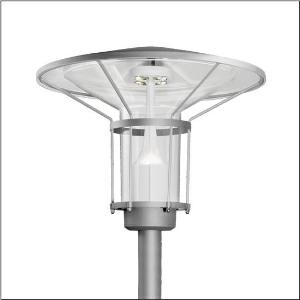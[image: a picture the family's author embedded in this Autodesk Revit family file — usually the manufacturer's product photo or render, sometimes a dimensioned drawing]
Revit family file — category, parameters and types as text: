
# Revit family: laterne_classic_iq___pl1_2s_5xa5245cf14h_6b83
name_source: partatom
category: Lighting Fixtures
units: mm (PartAtom-declared; Revit-internal decimal feet)

## family parameters
Cut with Voids When Loaded = No
Host = Face
Light Source = No
Part Type = Normal
Room Calculation Point = No
Round Connector Dimension = Use Diameter
Shared = No

## types (1)
- --- (1 x LED, 2670 lm, 23.9 W, 2200K)
    Apparent Load = 24 VA
    CIE Flux Codes = 21 60 93 97 100
    Color Rendering = 70
    Color Temperature = 2200K
    Default Elevation = 1800 mm
    Description = Lantern Classic iQ, mast luminaire, Module 540 iQ-SR, primary light control with 3 zone facetted reflector, of plastic, silver coated, highly specular, structured, primary optical cover: cover, of PMMA, transparent, light distribution: PL1.2s, light emission: direct distribution, primary light characteristic: symmetric, installation type: post-top, LED, High Power LED, rated luminous flux: 2.670lm, luminous efficacy: 112lm/W, light colour: 722, colour temperature: 2200K, control gear: ECG iQ, control: pre-setting: logarithmic dimming characteristic, Street-Remote, Auto-Match, Temp-Guard, Lumen-Switch, Night-Set, Smart-Wire, Light-Fading, Desk-Remote (wireless, voltage-free reading and setting of iQ features in the workshop via application-optimized NFC function/RFID function), optimised constant luminous flux control (CLO 2.0), with terminal, 6-pole, max. 2.5mm², mains connection: 230..240V, AC, 50/60Hz, start of lifetime: 24W, end of service life: 26W, reduction: 12W, luminaire housing, upper part, of glass-fibre reinforced polyester, coated, Siteco® metallic grey (DB 702S), diameter: 750mm, height: 596mm, spigot size: d x l = 76 x 70mm (post-top) | with reducer (optional accessory) 60 x 70mm, post-top mast mounting element, of diecast aluminium, coated, Siteco® metallic grey (DB 702S), Module 540 iQ-SR, traffic white (RAL 9016), equipment: standard, protection rating (complete): IP65, insulation class (complete): insulation class II (safety insulation), certification: CE, ENEC, VDE, packaging unit: 1 piece

Light Distribution: PL1.2s
    Height = 596 mm
    Lamp = 1 x LED
    Lamp Light Flux = 2670 lm
    Lamp Power = 23.9 W
    Lamp count = 1
    Length = 750 mm
    Luminous efficacy = 112 lm/W
    Manufacturer = Siteco
    ModVariant = No
    Model = 5XA5245CF14H
    Number of Poles = 1
    OnlyDefault = Yes
    Power Factor = 1
    Product Name = Laterne Classic iQ | PL1.2s
    Product group = mast luminaire | pylon top
    ProductGroupID = 6100
    Protection Class = Protection class II
    Protection Degree = IP 65
    RLX_Detail_Level = 1
    RLX_Emergency_Light_Flux = 0 lm
    RLX_Emergency_Type = 0
    RLX_Emergency_Type_DB = No
    RlxData = <blob elided: 62533 chars, md5=dc739e20>
    Socket = socket
    Standby Power = 0 W
    System Light Flux = 2670 lm
    System Power = 24 W
    Type Comments = factory setting: luminous flux: 100 % | dim-lin: 254 | 499 mA
    Type Image = l_1006052.jpg
    URL = http://relux.com
    VarID = @adj_115705
    Voltage = 0 V
    Weight = 0.00 kg
    Width = 0 mm  [stored 0 ft]

note: [stored X ft] marks values corroborated as IEEE doubles in the binary element streams (Revit-internal decimal feet)

## geometry (parser evidence)
native form markers: Blend x4, Sweep x10
no freeform markers — native parametric forms only
